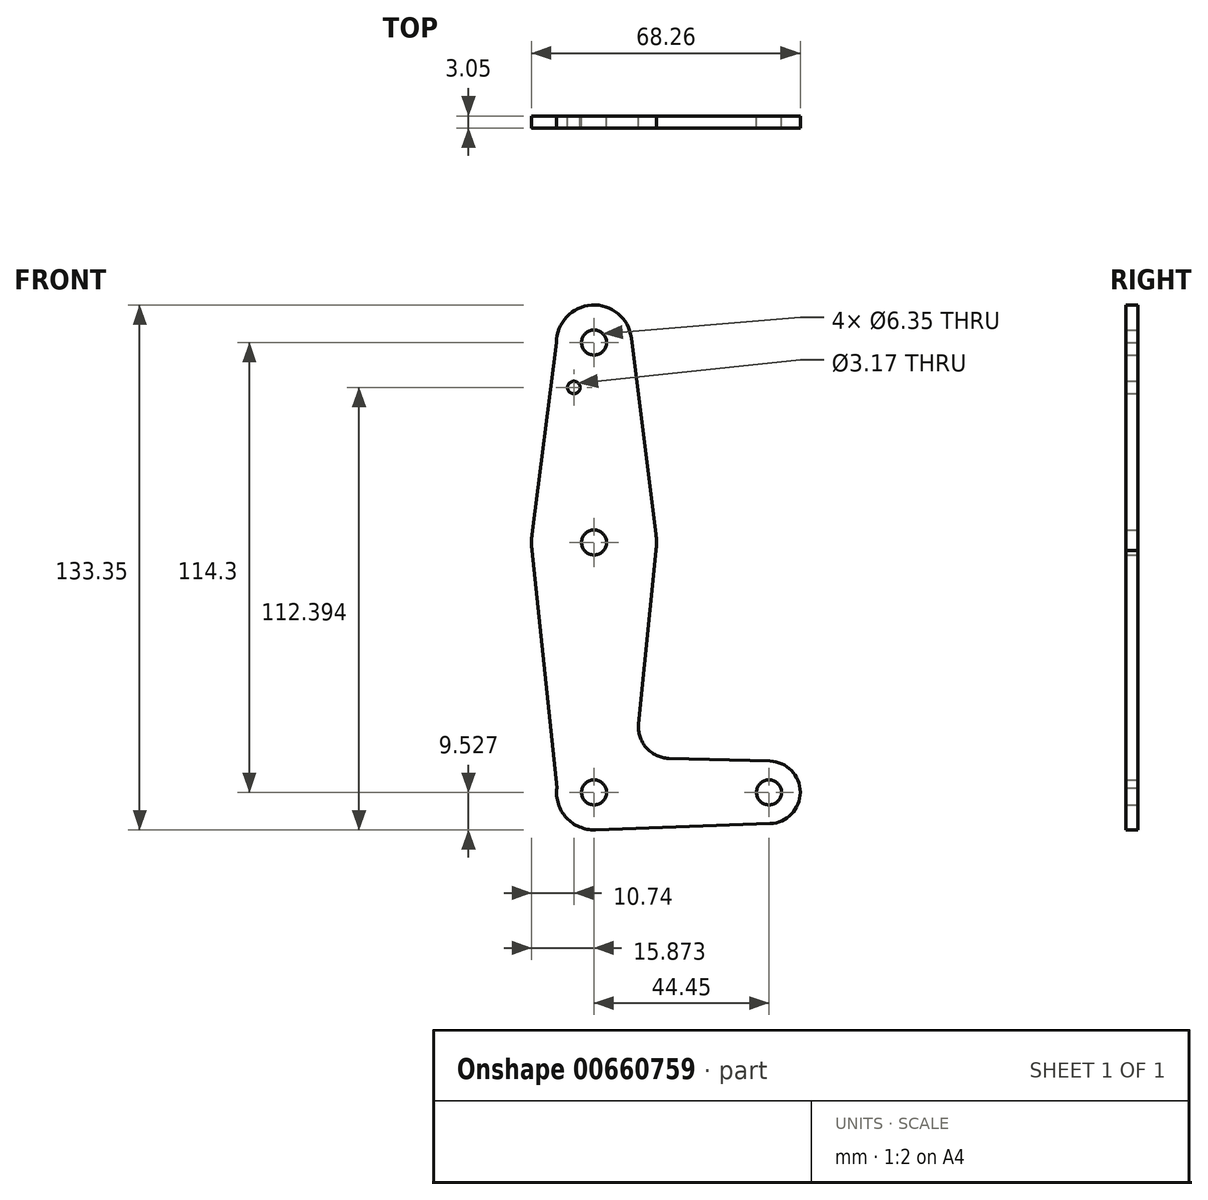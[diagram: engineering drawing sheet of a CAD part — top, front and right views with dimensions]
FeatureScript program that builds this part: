
annotation { "Feature Type Name" : "Feature", "Feature Type Description" : "" }
export const myFeature = defineFeature(function(context is Context, id is Id, definition is map)
    precondition{}
    {
        {
            var Q0;
            Q0=qCreatedBy(makeId("Front.planeOp"),FACE);
            var sketch = newSketch(context, id + "F0", { "sketchPlane" : qUnion([Q0])});
            skLineSegment(sketch, "E0", {"start": v(-51.5, 66.05) * mm, "end": v(-51.5, -48.25) * mm, "construction": true});
            skLineSegment(sketch, "E1", {"start": v(-51.5, -48.25) * mm, "end": v(-7.06, -48.25) * mm, "construction": true});
            skCircle(sketch, "E2", {"center": v(-51.5, 66.05) * mm, "radius": 9.53 * mm});
            skCircle(sketch, "E3", {"center": v(-51.5, 15.25) * mm, "radius": 15.88 * mm});
            skCircle(sketch, "E4", {"center": v(-51.5, -48.25) * mm, "radius": 9.53 * mm});
            skCircle(sketch, "E5", {"center": v(-7.06, -48.25) * mm, "radius": 7.94 * mm});
            skCircle(sketch, "E6", {"center": v(-51.5, 66.05) * mm, "radius": 0.57 * mm, "construction": true});
            skLineSegment(sketch, "E7", {"start": v(-61.03, 66) * mm, "end": v(-67.25, 17.26) * mm});
            skLineSegment(sketch, "E8", {"start": v(-67.25, 13.24) * mm, "end": v(-60.97, -47.16) * mm});
            skLineSegment(sketch, "E9", {"start": v(-42.06, 67.24) * mm, "end": v(-35.76, 17.23) * mm});
            skLineSegment(sketch, "E10", {"start": v(-35.76, 13.26) * mm, "end": v(-40.19, -30.86) * mm});
            skLineSegment(sketch, "E11", {"start": v(-32.5, -39.6) * mm, "end": v(-6.83, -40.32) * mm});
            skLineSegment(sketch, "E12", {"start": v(-51.2, -57.77) * mm, "end": v(-6.77, -56.19) * mm});
            skCircle(sketch, "E13", {"center": v(-51.5, 66.05) * mm, "radius": 3.18 * mm});
            skCircle(sketch, "E14", {"center": v(-51.5, 15.25) * mm, "radius": 3.18 * mm});
            skCircle(sketch, "E15", {"center": v(-51.5, -48.25) * mm, "radius": 3.18 * mm});
            skCircle(sketch, "E16", {"center": v(-7.06, -48.25) * mm, "radius": 3.18 * mm});
            skCircle(sketch, "E17", {"center": v(-56.64, 54.61) * mm, "radius": 1.59 * mm});
            skArc(sketch, "E18.filletArc", {"start": v(-40.19, -30.86) * mm, "mid": v(-38.25, -36.9) * mm, "end": v(-32.5, -39.6) * mm});
            skText(sketch, "E19", { "text": "Dylon Bonsall Volume: 704 in^3", "fontName": "OpenSans-Regular.ttf"});
            const initialGuessF0  = {"E19": [-0.00452, 0.05388, 1, 0, 0.01437]};
            skSetInitialGuess(sketch, initialGuessF0);
            skSolve(sketch);
        }
        {
            var Q0;
            {var subQ0=sQuery(id+"F0.wireOp",EDGE,"E8");Q0=makeQuery(id+"F0.imprint","IMPRINT",FACE,{"disambiguationData":[TD([[makeQuery(id+"F0.imprint","IMPRINT",EDGE,{"derivedFrom":subQ0}),1.0]])]});}
            var Q1;
            {var subQ0=sQuery(id+"F0.wireOp",EDGE,"E7");Q1=makeQuery(id+"F0.imprint","IMPRINT",FACE,{"disambiguationData":[TD([[makeQuery(id+"F0.imprint","IMPRINT",EDGE,{"derivedFrom":subQ0}),1.0]])]});}
            var Q2;
            Q2=makeQuery(id+"F0.imprint","IMPRINT",FACE,{"disambiguationData":[TD([[makeQuery(id+"F0.imprint","IMPRINT",EDGE,{"derivedFrom":sQuery(id+"F0.wireOp",EDGE,"E14")}),-1.0]])]});
            var Q3;
            Q3=makeQuery(id+"F0.imprint","IMPRINT",FACE,{"disambiguationData":[TD([[makeQuery(id+"F0.imprint","IMPRINT",EDGE,{"derivedFrom":sQuery(id+"F0.wireOp",EDGE,"E13")}),-1.0]])]});
            var Q4;
            Q4=makeQuery(id+"F0.imprint","IMPRINT",FACE,{"disambiguationData":[TD([[makeQuery(id+"F0.imprint","IMPRINT",EDGE,{"derivedFrom":sQuery(id+"F0.wireOp",EDGE,"E15")}),-1.0]])]});
            var Q5;
            Q5=makeQuery(id+"F0.imprint","IMPRINT",FACE,{"disambiguationData":[TD([[makeQuery(id+"F0.imprint","IMPRINT",EDGE,{"derivedFrom":sQuery(id+"F0.wireOp",EDGE,"E16")}),-1.0]])]});
            extrude(context, id + "F1", {"entities" : qUnion([Q0, Q1, Q2, Q3, Q4, Q5]), "depth" : 3.05 * mm, "offsetDistance" : 25.4 * mm});
        }
    });
